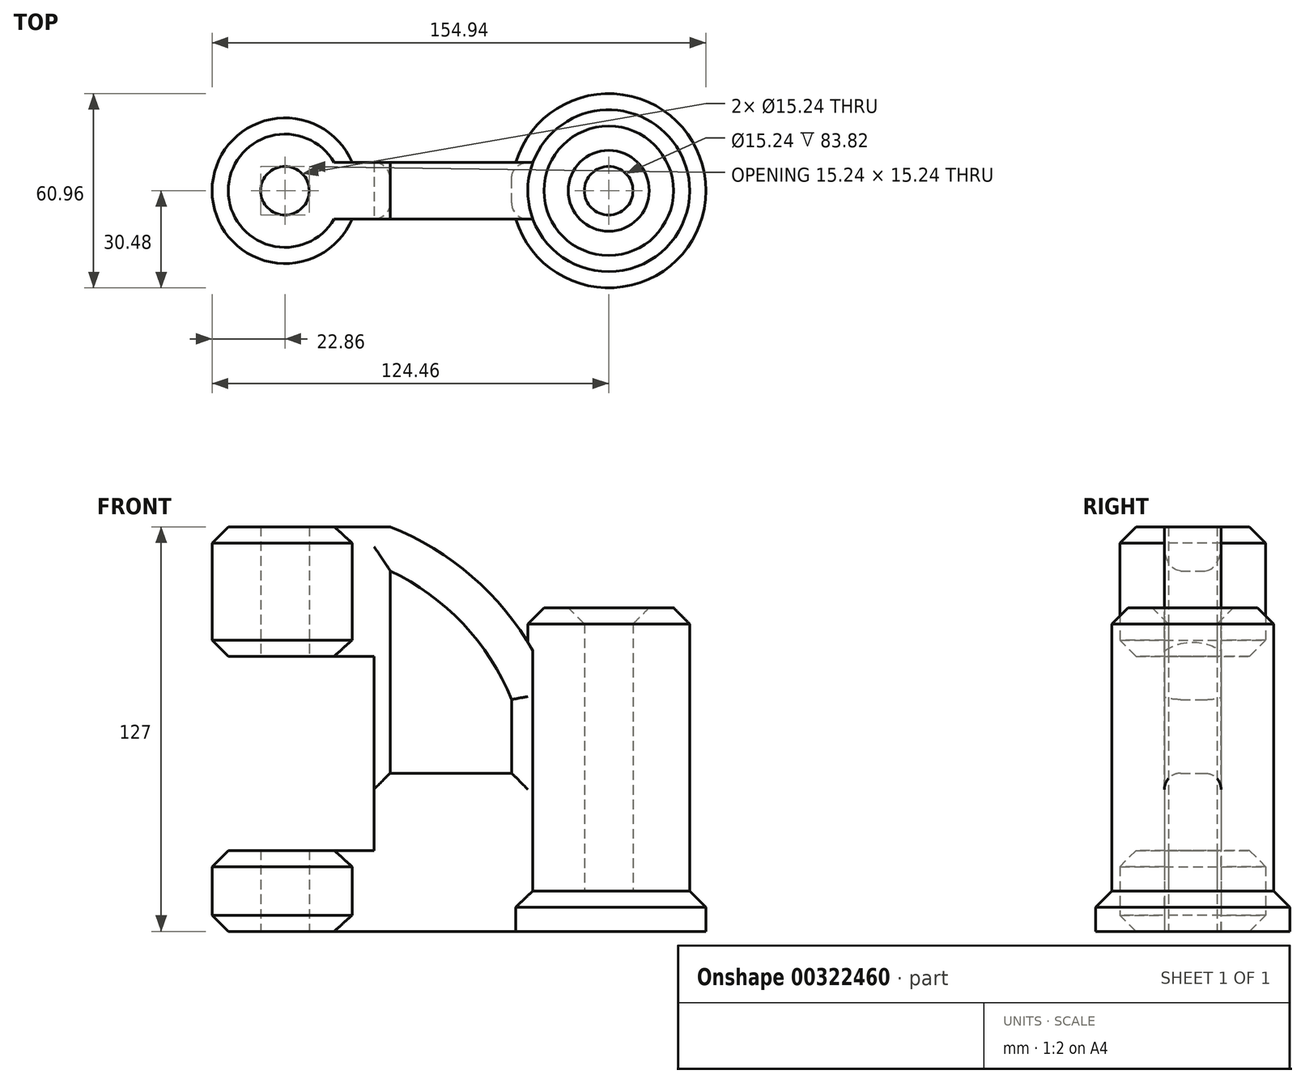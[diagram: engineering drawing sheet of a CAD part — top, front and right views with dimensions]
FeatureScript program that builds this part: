
annotation { "Feature Type Name" : "Feature", "Feature Type Description" : "" }
export const myFeature = defineFeature(function(context is Context, id is Id, definition is map)
    precondition{}
    {
        {
            var Q0;
            Q0=qCreatedBy(makeId("Top.planeOp"),FACE);
            var sketch = newSketch(context, id + "F0", { "sketchPlane" : qUnion([Q0])});
            skCircle(sketch, "E0", {"center": v(0, 0) * mm, "radius": 25.4 * mm});
            skCircle(sketch, "E1", {"center": v(0, 0) * mm, "radius": 7.62 * mm});
            skCircle(sketch, "E2", {"center": v(-101.6, 0) * mm, "radius": 22.86 * mm});
            skCircle(sketch, "E3", {"center": v(-101.6, 0) * mm, "radius": 7.62 * mm});
            skSolve(sketch);
        }
        {
            var Q0;
            Q0=makeQuery(id+"F0.imprint","IMPRINT",FACE,{"disambiguationData":[TD([[makeQuery(id+"F0.imprint","IMPRINT",EDGE,{"derivedFrom":sQuery(id+"F0.wireOp",EDGE,"E2")}),1.0]])]});
            extrude(context, id + "F1", {"entities" : qUnion([Q0]), "depth" : 127 * mm});
        }
        {
            var Q0;
            Q0=makeQuery(id+"F0.imprint","IMPRINT",FACE,{"disambiguationData":[TD([[makeQuery(id+"F0.imprint","IMPRINT",EDGE,{"derivedFrom":sQuery(id+"F0.wireOp",EDGE,"E0")}),1.0]])]});
            extrude(context, id + "F2", {"entities" : qUnion([Q0]), "depth" : 101.6 * mm});
        }
        {
            var Q0;
            Q0=qCreatedBy(makeId("Front.planeOp"),FACE);
            var sketch = newSketch(context, id + "F3", { "sketchPlane" : qUnion([Q0])});
            skLineSegment(sketch, "E4", {"start": v(-81.28, 0) * mm, "end": v(-81.28, 127) * mm});
            skLineSegment(sketch, "E5", {"start": v(-20.32, 81.28) * mm, "end": v(-20.32, 0) * mm});
            skLineSegment(sketch, "E6", {"start": v(-20.32, 0) * mm, "end": v(-81.28, 0) * mm});
            skLineSegment(sketch, "E7", {"start": v(-81.28, 127) * mm, "end": v(-68.58, 127) * mm});
            skArc(sketch, "E8", {"start": v(-20.32, 81.28) * mm, "mid": v(-40.02, 108.82) * mm, "end": v(-68.58, 127) * mm});
            skArc(sketch, "E9.0", {"start": v(-30.48, 72.77) * mm, "mid": v(-45.72, 96.56) * mm, "end": v(-68.58, 113.17) * mm});
            skLineSegment(sketch, "E10", {"start": v(-68.58, 113.17) * mm, "end": v(-68.58, 49.67) * mm});
            skLineSegment(sketch, "E11", {"start": v(-68.58, 49.67) * mm, "end": v(-30.48, 49.67) * mm});
            skLineSegment(sketch, "E12", {"start": v(-30.48, 49.67) * mm, "end": v(-30.48, 72.77) * mm});
            skSolve(sketch);
        }
        {
            var Q0;
            Q0=makeQuery(id+"F3.imprint","IMPRINT",FACE,{"disambiguationData":[TD([[makeQuery(id+"F3.imprint","IMPRINT",EDGE,{"derivedFrom":sQuery(id+"F3.wireOp",EDGE,"E4")}),-1.0]])]});
            extrude(context, id + "F4", {"entities" : qUnion([Q0]), "operationType" : NewBodyOperationType.ADD, "depth" : 17.78 * mm, "symmetric" : true});
        }
        {
            var Q0;
            Q0=qCreatedBy(makeId("Front.planeOp"),FACE);
            var sketch = newSketch(context, id + "F5", { "sketchPlane" : qUnion([Q0])});
            skLineSegment(sketch, "E13.bottom", {"start": v(-134.62, 86.36) * mm, "end": v(-73.66, 86.36) * mm});
            skLineSegment(sketch, "E13.top", {"start": v(-134.62, 25.4) * mm, "end": v(-73.66, 25.4) * mm});
            skLineSegment(sketch, "E13.left", {"start": v(-134.62, 86.36) * mm, "end": v(-134.62, 25.4) * mm});
            skLineSegment(sketch, "E13.right", {"start": v(-73.66, 86.36) * mm, "end": v(-73.66, 25.4) * mm});
            skSolve(sketch);
        }
        {
            var Q0;
            Q0 = qSketchRegion(id + "F5", true);
            extrude(context, id + "F6", {"entities" : qUnion([Q0]), "operationType" : NewBodyOperationType.REMOVE, "oppositeDirection" : true, "depth" : 101.6 * mm, "symmetric" : true});
        }
        {
            var Q0;
            Q0=makeQuery(id+"F4.opExtrude","CAP_EDGE",EDGE,{"disambiguationData":[OSD([sQuery(id+"F3.wireOp",EDGE,"E9.0")])],"isStart":false});
            var Q1;
            Q1=makeQuery(id+"F4.opExtrude","CAP_EDGE",EDGE,{"disambiguationData":[OSD([sQuery(id+"F3.wireOp",EDGE,"E12")])],"isStart":false});
            var Q2;
            Q2=makeQuery(id+"F4.opExtrude","CAP_EDGE",EDGE,{"disambiguationData":[OSD([sQuery(id+"F3.wireOp",EDGE,"E11")])],"isStart":false});
            var Q3;
            Q3=makeQuery(id+"F4.opExtrude","CAP_EDGE",EDGE,{"disambiguationData":[OSD([sQuery(id+"F3.wireOp",EDGE,"E10")])],"isStart":false});
            var Q4;
            Q4=makeQuery(id+"F4.opExtrude","CAP_EDGE",EDGE,{"disambiguationData":[OSD([sQuery(id+"F3.wireOp",EDGE,"E9.0")])],"isStart":true});
            var Q5;
            Q5=makeQuery(id+"F4.opExtrude","CAP_EDGE",EDGE,{"disambiguationData":[OSD([sQuery(id+"F3.wireOp",EDGE,"E12")])],"isStart":true});
            var Q6;
            Q6=makeQuery(id+"F4.opExtrude","CAP_EDGE",EDGE,{"disambiguationData":[OSD([sQuery(id+"F3.wireOp",EDGE,"E11")])],"isStart":true});
            var Q7;
            Q7=makeQuery(id+"F4.opExtrude","CAP_EDGE",EDGE,{"disambiguationData":[OSD([sQuery(id+"F3.wireOp",EDGE,"E10")])],"isStart":true});
            fillet(context, id + "F7", {"entities" : qUnion([Q0, Q1, Q2, Q3, Q4, Q5, Q6, Q7]), "radius" : 5.08 * mm, "tangentPropagation" : true, "allowEdgeOverflow" : false});
        }
        {
            var Q0;
            Q0=makeQuery(id+"F6.boolean.opBoolean","INTERSECT",EDGE,{"derivedFrom":[makeQuery(id+"F1.opExtrude","SWEPT_FACE",FACE,{"disambiguationData":[OSD([sQuery(id+"F0.wireOp",EDGE,"E2")])]}),makeQuery(id+"F6.opExtrude","SWEPT_FACE",FACE,{"disambiguationData":[OSD([sQuery(id+"F5.wireOp",EDGE,"E13.bottom")])]})]});
            var Q1;
            Q1=makeQuery(id+"F1.opExtrude","CAP_EDGE",EDGE,{"disambiguationData":[OSD([sQuery(id+"F0.wireOp",EDGE,"E2")])],"isStart":true});
            var Q2;
            Q2=makeQuery(id+"F6.boolean.opBoolean","INTERSECT",EDGE,{"derivedFrom":[makeQuery(id+"F1.opExtrude","SWEPT_FACE",FACE,{"disambiguationData":[OSD([sQuery(id+"F0.wireOp",EDGE,"E2")])]}),makeQuery(id+"F6.opExtrude","SWEPT_FACE",FACE,{"disambiguationData":[OSD([sQuery(id+"F5.wireOp",EDGE,"E13.top")])]})]});
            var Q3;
            Q3=makeQuery(id+"F1.opExtrude","CAP_EDGE",EDGE,{"disambiguationData":[OSD([sQuery(id+"F0.wireOp",EDGE,"E2")])],"isStart":false});
            chamfer(context, id + "F8", {"entities" : qUnion([Q0, Q1, Q2, Q3]), "width" : 5.08 * mm, "tangentPropagation" : true});
        }
        {
            var Q0;
            Q0=qCreatedBy(makeId("Top.planeOp"),FACE);
            var sketch = newSketch(context, id + "F9", { "sketchPlane" : qUnion([Q0])});
            skCircle(sketch, "E14.0", {"center": v(0, 0) * mm, "radius": 30.48 * mm});
            skLineSegment(sketch, "E15.0", {"start": v(-62.23, -2.54) * mm, "end": v(-31.65, -2.54) * mm});
            skLineSegment(sketch, "E15.1", {"start": v(-62.23, 2.54) * mm, "end": v(-62.23, -2.54) * mm});
            skLineSegment(sketch, "E15.2", {"start": v(-31.65, 2.54) * mm, "end": v(-62.23, 2.54) * mm});
            skArc(sketch, "E15.3", {"start": v(-31.65, -2.54) * mm, "mid": v(-31.75, 0) * mm, "end": v(-31.65, 2.54) * mm});
            skSolve(sketch);
        }
        {
            var Q0;
            Q0 = qSketchRegion(id + "F9", true);
            extrude(context, id + "F10", {"entities" : qUnion([Q0]), "operationType" : NewBodyOperationType.ADD, "depth" : 12.7 * mm});
        }
        {
            var Q0;
            Q0=makeQuery(id+"F10.opExtrude","CAP_EDGE",EDGE,{"disambiguationData":[OSD([sQuery(id+"F9.wireOp",EDGE,"E14.0")])],"isStart":false});
            var Q1;
            Q1=makeQuery(id+"F2.opExtrude","CAP_EDGE",EDGE,{"disambiguationData":[OSD([sQuery(id+"F0.wireOp",EDGE,"E0")])],"isStart":false});
            var Q2;
            Q2=makeQuery(id+"F2.opExtrude","CAP_EDGE",EDGE,{"disambiguationData":[OSD([sQuery(id+"F0.wireOp",EDGE,"E1")])],"isStart":false});
            chamfer(context, id + "F11", {"entities" : qUnion([Q0, Q1, Q2]), "width" : 5.08 * mm, "tangentPropagation" : true});
        }
    });
